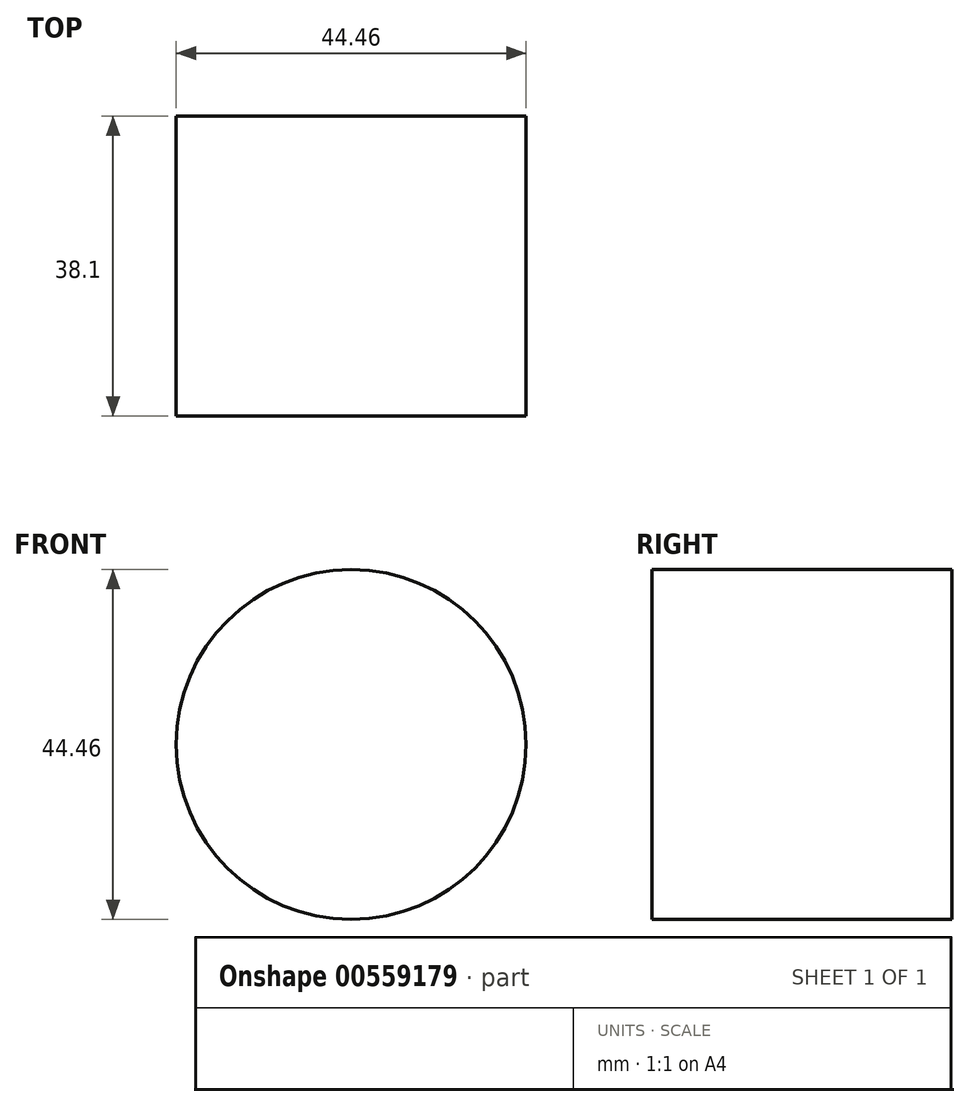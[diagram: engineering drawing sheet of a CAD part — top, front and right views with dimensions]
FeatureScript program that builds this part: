
annotation { "Feature Type Name" : "Feature", "Feature Type Description" : "" }
export const myFeature = defineFeature(function(context is Context, id is Id, definition is map)
    precondition{}
    {
        {
            var Q0;
            Q0=qCreatedBy(makeId("Front.planeOp"),FACE);
            var sketch = newSketch(context, id + "F0", { "sketchPlane" : qUnion([Q0])});
            skCircle(sketch, "E0", {"center": v(0, 0) * mm, "radius": 22.22 * mm});
            skSolve(sketch);
        }
        {
            var Q0;
            Q0 = qSketchRegion(id + "F0", true);
            extrude(context, id + "F1", {"entities" : qUnion([Q0]), "depth" : 38.1 * mm, "offsetDistance" : 25.4 * mm});
        }
    });
